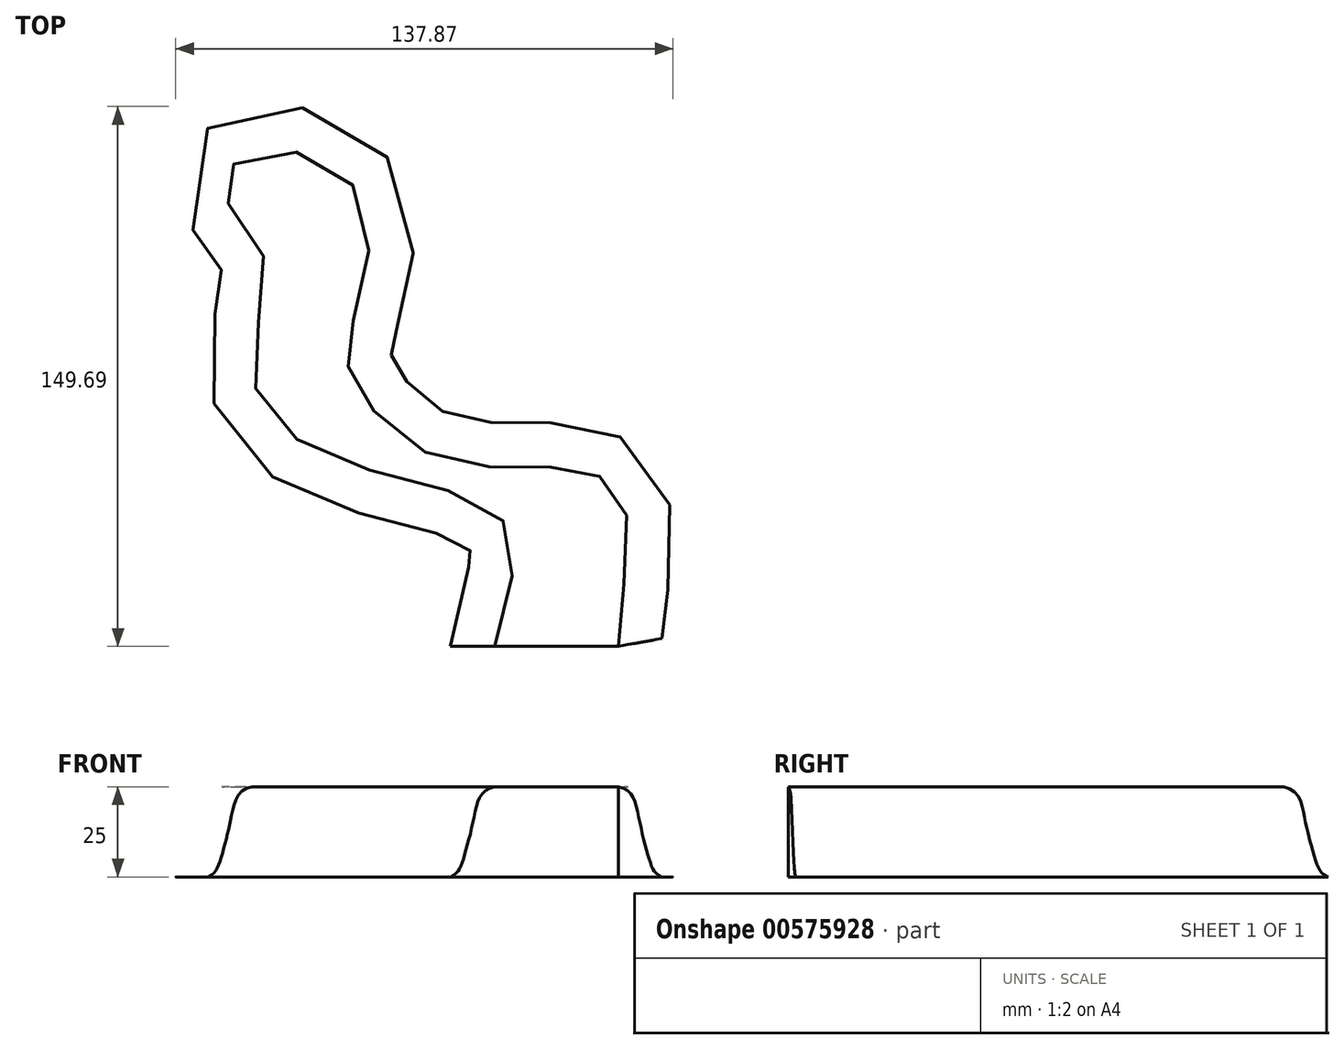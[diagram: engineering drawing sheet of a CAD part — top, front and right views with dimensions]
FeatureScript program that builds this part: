
annotation { "Feature Type Name" : "Feature", "Feature Type Description" : "" }
export const myFeature = defineFeature(function(context is Context, id is Id, definition is map)
    precondition{}
    {
        {
            var Q0;
            Q0=qCreatedBy(makeId("Top.planeOp"),FACE);
            var sketch = newSketch(context, id + "F0", { "sketchPlane" : qUnion([Q0])});
            skFitSpline(sketch, "E0", {"points": [v(37.38, -66.32) * mm, v(40.98, -36.25) * mm, v(29.92, -19.62) * mm, v(-12.7, -6.48) * mm, v(-31.87, 16.42) * mm, v(-28.85, 48.56) * mm, v(-40.75, 68.63) * mm, v(-21.75, 77.33) * mm, v(0, 59.57) * mm, v(-4.88, 26.1) * mm, v(-3.77, 13.76) * mm, v(14.67, -5.5) * mm, v(44.3, -10.39) * mm, v(63.66, -12.52) * mm, v(72.36, -26.37) * mm, v(69.52, -58.69) * mm, v(68.8, -66.32) * mm, v(37.38, -66.32) * mm]});
            skSolve(sketch);
        }
        {
            var Q0;
            Q0 = qSketchRegion(id + "F0", true);
            extrude(context, id + "F1", {"entities" : qUnion([Q0]), "depth" : 25 * mm, "offsetDistance" : 25 * mm});
        }
        {
            var Q0;
            Q0=qCreatedBy(makeId("Front.planeOp"),FACE);
            cPlane(context, id + "F2", {"entities" : qUnion([Q0]), "cplaneType" : CPlaneType.OFFSET, "offset" : 60 * mm, "width" : 150 * mm, "height" : 150 * mm});
        }
        {
            var Q0;
            Q0=qCreatedBy(id+"F2.planeOp",FACE);
            var sketch = newSketch(context, id + "F3", { "sketchPlane" : qUnion([Q0])});
            skLineSegment(sketch, "E1.bottom", {"start": v(11.95, 30.14) * mm, "end": v(123.38, 30.14) * mm});
            skLineSegment(sketch, "E1.top", {"start": v(11.95, -10.6) * mm, "end": v(123.38, -10.6) * mm});
            skLineSegment(sketch, "E1.left", {"start": v(11.95, 30.14) * mm, "end": v(11.95, -10.6) * mm});
            skLineSegment(sketch, "E1.right", {"start": v(123.38, 30.14) * mm, "end": v(123.38, -10.6) * mm});
            skSolve(sketch);
        }
        {
            var Q0;
            Q0 = qSketchRegion(id + "F3", true);
            extrude(context, id + "F4", {"entities" : qUnion([Q0]), "operationType" : NewBodyOperationType.REMOVE, "depth" : 25 * mm, "offsetDistance" : 25 * mm});
        }
        {
            var Q0;
            Q0=makeQuery(id+"F4.boolean.opBoolean","COPY",FACE,{"derivedFrom":makeQuery(id+"F4.opExtrude","CAP_FACE",FACE,{"disambiguationData":[OSD([sQuery(id+"F3.wireOp",EDGE,"E1.bottom"),sQuery(id+"F3.wireOp",EDGE,"E1.top"),sQuery(id+"F3.wireOp",EDGE,"E1.left"),sQuery(id+"F3.wireOp",EDGE,"E1.right")])],"isStart":true})});
            var sketch = newSketch(context, id + "F5", { "sketchPlane" : qUnion([Q0])});
            skFitSpline(sketch, "E2", {"points": [v(35.4, 25) * mm, v(29.56, 16.24) * mm, v(26.19, 3.52) * mm, v(23.09, 0) * mm], "startDerivative": vector(-36.85, -5.54) * mm, "endDerivative": vector(-25.04, -12.35) * mm});
            skLineSegment(sketch, "E3", {"start": v(23.09, 0) * mm, "end": v(35.4, 0) * mm});
            skLineSegment(sketch, "E4", {"start": v(35.4, 0) * mm, "end": v(35.4, 25) * mm});
            skSolve(sketch);
        }
        {
            var Q0;
            Q0 = qSketchRegion(id + "F5", true);
            var Q1;
            Q1=makeQuery(id+"F1.opExtrude","CAP_EDGE",EDGE,{"disambiguationData":[OSD([sQuery(id+"F0.wireOp",EDGE,"E0")])],"isStart":false});
            sweep(context, id + "F6", {"operationType" : NewBodyOperationType.ADD, "profiles" : qUnion([Q0]), "path" : qUnion([Q1])});
        }
    });
